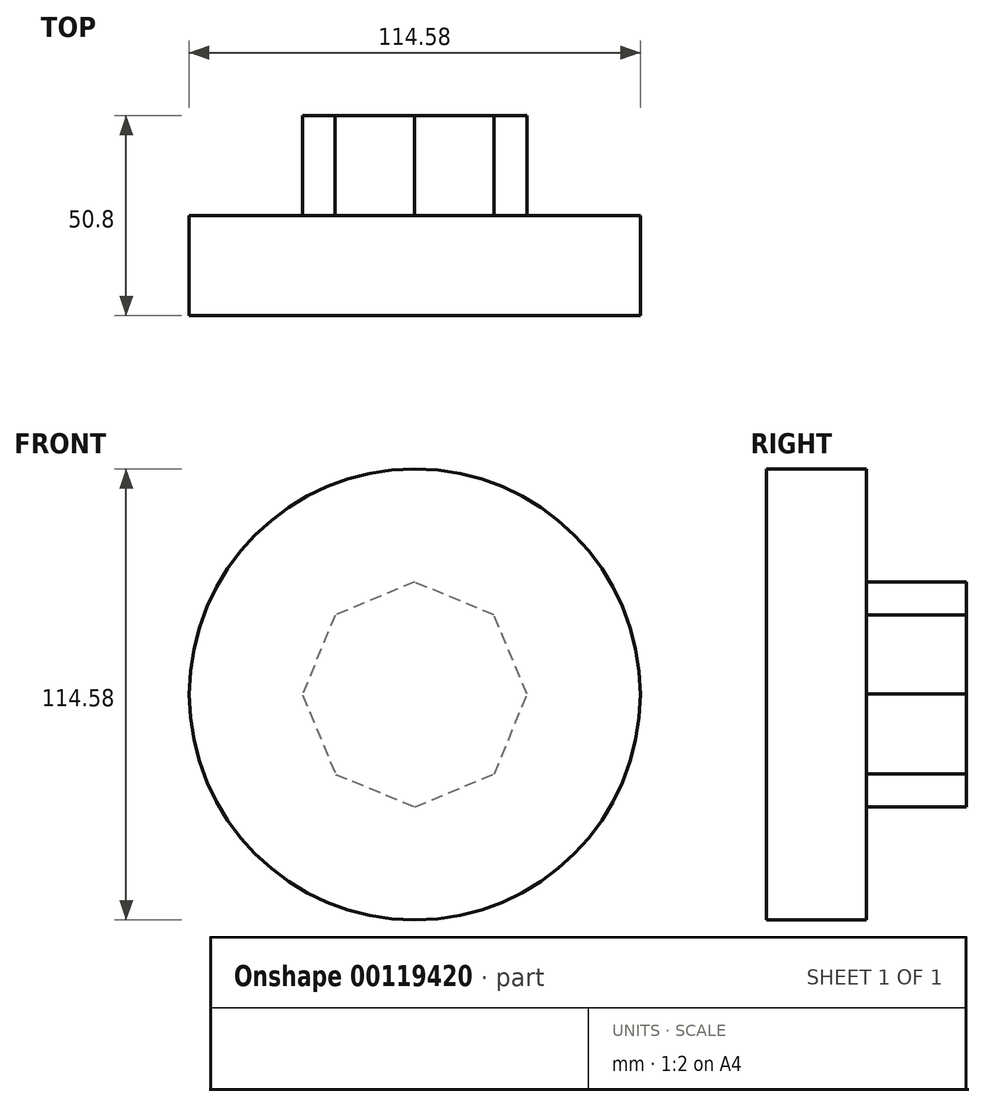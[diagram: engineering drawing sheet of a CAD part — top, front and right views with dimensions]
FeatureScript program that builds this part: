
annotation { "Feature Type Name" : "Feature", "Feature Type Description" : "" }
export const myFeature = defineFeature(function(context is Context, id is Id, definition is map)
    precondition{}
    {
        {
            var Q0;
            Q0=qCreatedBy(makeId("Front.planeOp"),FACE);
            var sketch = newSketch(context, id + "F0", { "sketchPlane" : qUnion([Q0])});
            skCircle(sketch, "E0", {"center": v(0, 0) * mm, "radius": 57.29 * mm});
            skSolve(sketch);
        }
        {
            var Q0;
            Q0=makeQuery(id+"F0.imprint","IMPRINT",FACE,{"disambiguationData":[TD([[makeQuery(id+"F0.imprint","IMPRINT",EDGE,{"derivedFrom":sQuery(id+"F0.wireOp",EDGE,"E0")}),1.0]])]});
            extrude(context, id + "F1", {"entities" : qUnion([Q0]), "depth" : 25.4 * mm});
        }
        {
            var Q0;
            Q0=makeQuery(id+"F1.opExtrude","CAP_FACE",FACE,{"disambiguationData":[OSD([sQuery(id+"F0.wireOp",EDGE,"E0")])],"isStart":true});
            var sketch = newSketch(context, id + "F2", { "sketchPlane" : qUnion([Q0])});
            skCircle(sketch, "E1.cCircle", {"center": v(0, 0) * mm, "radius": 26.39 * mm, "construction": true});
            skLineSegment(sketch, "E1.0", {"start": v(-20.13, 20.26) * mm, "end": v(0.1, 28.56) * mm});
            skLineSegment(sketch, "E1.1", {"start": v(0.1, 28.56) * mm, "end": v(20.26, 20.13) * mm});
            skLineSegment(sketch, "E1.2", {"start": v(20.26, 20.13) * mm, "end": v(28.56, -0.1) * mm});
            skLineSegment(sketch, "E1.3", {"start": v(28.56, -0.1) * mm, "end": v(20.13, -20.26) * mm});
            skLineSegment(sketch, "E1.4", {"start": v(20.13, -20.26) * mm, "end": v(-0.1, -28.56) * mm});
            skLineSegment(sketch, "E1.5", {"start": v(-0.1, -28.56) * mm, "end": v(-20.26, -20.13) * mm});
            skLineSegment(sketch, "E1.6", {"start": v(-20.26, -20.13) * mm, "end": v(-28.56, 0.1) * mm});
            skLineSegment(sketch, "E1.7", {"start": v(-28.56, 0.1) * mm, "end": v(-20.13, 20.26) * mm});
            skPoint(sketch, "E1.0.midPoint", {"position": v(-10.02, 24.4) * mm});
            skSolve(sketch);
        }
        {
            var Q0;
            Q0 = qSketchRegion(id + "F2", true);
            extrude(context, id + "F3", {"entities" : qUnion([Q0]), "operationType" : NewBodyOperationType.ADD, "depth" : 25.4 * mm});
        }
    });
